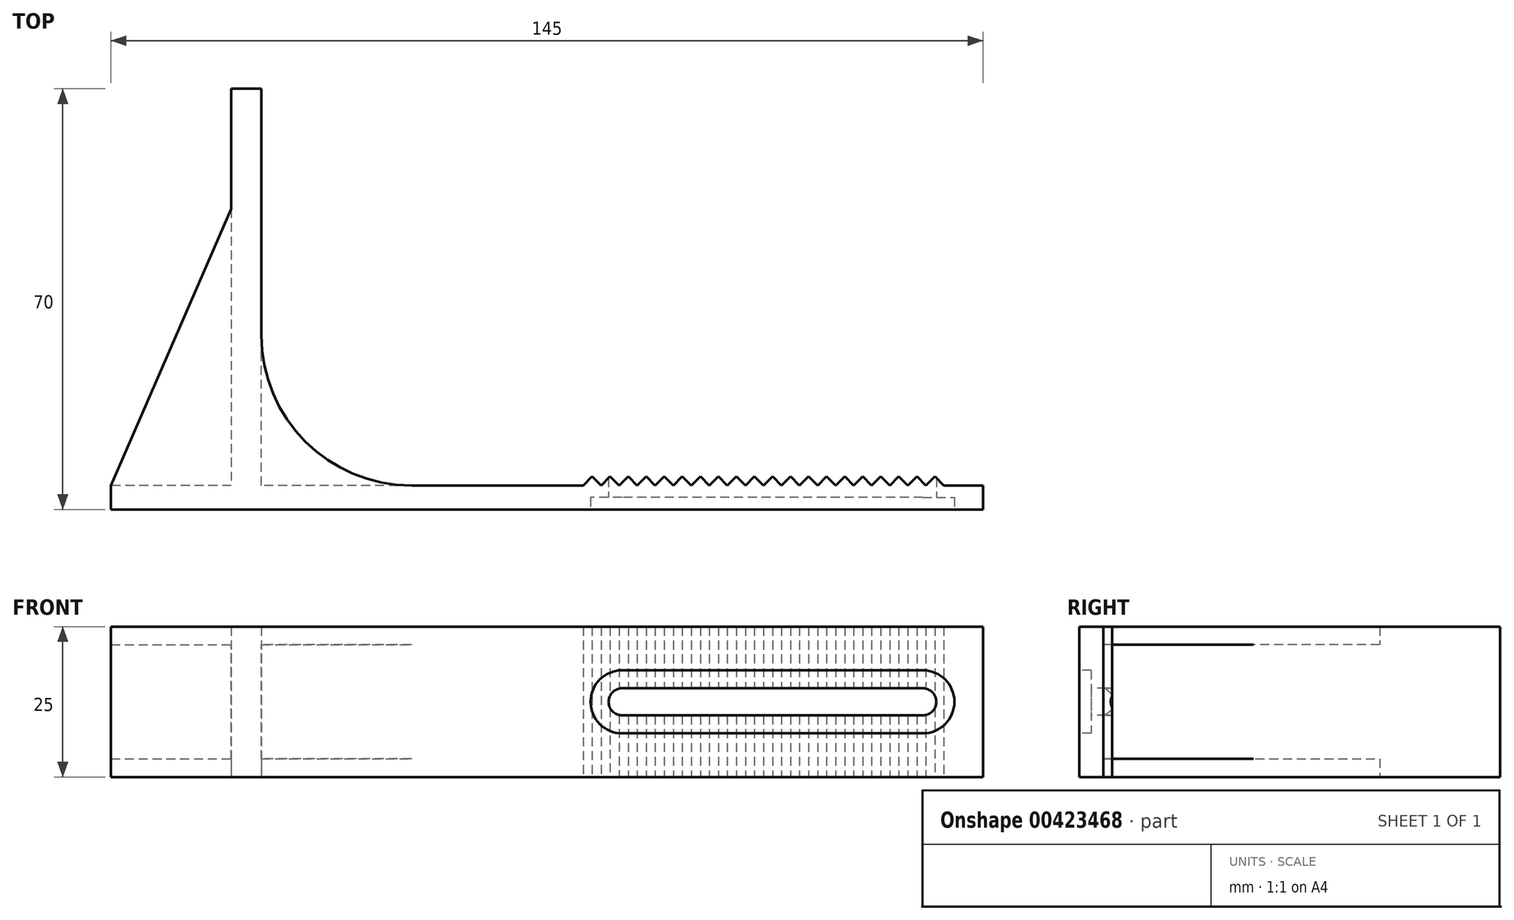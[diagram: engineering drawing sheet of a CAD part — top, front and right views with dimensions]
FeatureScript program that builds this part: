
annotation { "Feature Type Name" : "Feature", "Feature Type Description" : "" }
export const myFeature = defineFeature(function(context is Context, id is Id, definition is map)
    precondition{}
    {
        {
            var Q0;
            Q0=qCreatedBy(makeId("Top.planeOp"),FACE);
            var sketch = newSketch(context, id + "F0", { "sketchPlane" : qUnion([Q0])});
            skLineSegment(sketch, "E0.bottom", {"start": v(25, 0) * mm, "end": v(53.5, 0) * mm});
            skLineSegment(sketch, "E0.top", {"start": v(-25, -4) * mm, "end": v(120, -4) * mm});
            skLineSegment(sketch, "E0.right", {"start": v(120, 0) * mm, "end": v(120, -4) * mm});
            skLineSegment(sketch, "E1.top", {"start": v(0, 66) * mm, "end": v(-5, 66) * mm});
            skLineSegment(sketch, "E1.left", {"start": v(0, 25) * mm, "end": v(0, 66) * mm});
            skLineSegment(sketch, "E1.right", {"start": v(-5, 46) * mm, "end": v(-5, 66) * mm});
            skLineSegment(sketch, "E2", {"start": v(53.5, 0) * mm, "end": v(55, 1.5) * mm});
            skLineSegment(sketch, "E3", {"start": v(55, 1.5) * mm, "end": v(56.5, 0) * mm});
            skLineSegment(sketch, "E4.1.0.0", {"start": v(56.5, 0) * mm, "end": v(58, 1.5) * mm});
            skLineSegment(sketch, "E4.1.0.1", {"start": v(58, 1.5) * mm, "end": v(59.5, 0) * mm});
            skLineSegment(sketch, "E4.2.0.0", {"start": v(59.5, 0) * mm, "end": v(61, 1.5) * mm});
            skLineSegment(sketch, "E4.2.0.1", {"start": v(61, 1.5) * mm, "end": v(62.5, 0) * mm});
            skLineSegment(sketch, "E4.3.0.0", {"start": v(62.5, 0) * mm, "end": v(64, 1.5) * mm});
            skLineSegment(sketch, "E4.3.0.1", {"start": v(64, 1.5) * mm, "end": v(65.5, 0) * mm});
            skLineSegment(sketch, "E4.4.0.0", {"start": v(65.5, 0) * mm, "end": v(67, 1.5) * mm});
            skLineSegment(sketch, "E4.4.0.1", {"start": v(67, 1.5) * mm, "end": v(68.5, 0) * mm});
            skLineSegment(sketch, "E4.5.0.0", {"start": v(68.5, 0) * mm, "end": v(70, 1.5) * mm});
            skLineSegment(sketch, "E4.5.0.1", {"start": v(70, 1.5) * mm, "end": v(71.5, 0) * mm});
            skLineSegment(sketch, "E4.6.0.0", {"start": v(71.5, 0) * mm, "end": v(73, 1.5) * mm});
            skLineSegment(sketch, "E4.6.0.1", {"start": v(73, 1.5) * mm, "end": v(74.5, 0) * mm});
            skLineSegment(sketch, "E4.7.0.0", {"start": v(74.5, 0) * mm, "end": v(76, 1.5) * mm});
            skLineSegment(sketch, "E4.7.0.1", {"start": v(76, 1.5) * mm, "end": v(77.5, 0) * mm});
            skLineSegment(sketch, "E4.8.0.0", {"start": v(77.5, 0) * mm, "end": v(79, 1.5) * mm});
            skLineSegment(sketch, "E4.8.0.1", {"start": v(79, 1.5) * mm, "end": v(80.5, 0) * mm});
            skLineSegment(sketch, "E4.9.0.0", {"start": v(80.5, 0) * mm, "end": v(82, 1.5) * mm});
            skLineSegment(sketch, "E4.9.0.1", {"start": v(82, 1.5) * mm, "end": v(83.5, 0) * mm});
            skLineSegment(sketch, "E4.10.0.0", {"start": v(83.5, 0) * mm, "end": v(85, 1.5) * mm});
            skLineSegment(sketch, "E4.10.0.1", {"start": v(85, 1.5) * mm, "end": v(86.5, 0) * mm});
            skLineSegment(sketch, "E4.11.0.0", {"start": v(86.5, 0) * mm, "end": v(88, 1.5) * mm});
            skLineSegment(sketch, "E4.11.0.1", {"start": v(88, 1.5) * mm, "end": v(89.5, 0) * mm});
            skLineSegment(sketch, "E4.12.0.0", {"start": v(89.5, 0) * mm, "end": v(91, 1.5) * mm});
            skLineSegment(sketch, "E4.12.0.1", {"start": v(91, 1.5) * mm, "end": v(92.5, 0) * mm});
            skLineSegment(sketch, "E4.13.0.0", {"start": v(92.5, 0) * mm, "end": v(94, 1.5) * mm});
            skLineSegment(sketch, "E4.13.0.1", {"start": v(94, 1.5) * mm, "end": v(95.5, 0) * mm});
            skLineSegment(sketch, "E4.14.0.0", {"start": v(95.5, 0) * mm, "end": v(97, 1.5) * mm});
            skLineSegment(sketch, "E4.14.0.1", {"start": v(97, 1.5) * mm, "end": v(98.5, 0) * mm});
            skLineSegment(sketch, "E4.15.0.0", {"start": v(98.5, 0) * mm, "end": v(100, 1.5) * mm});
            skLineSegment(sketch, "E4.15.0.1", {"start": v(100, 1.5) * mm, "end": v(101.5, 0) * mm});
            skLineSegment(sketch, "E4.16.0.0", {"start": v(101.5, 0) * mm, "end": v(103, 1.5) * mm});
            skLineSegment(sketch, "E4.16.0.1", {"start": v(103, 1.5) * mm, "end": v(104.5, 0) * mm});
            skLineSegment(sketch, "E4.17.0.0", {"start": v(104.5, 0) * mm, "end": v(106, 1.5) * mm});
            skLineSegment(sketch, "E4.17.0.1", {"start": v(106, 1.5) * mm, "end": v(107.5, 0) * mm});
            skLineSegment(sketch, "E4.18.0.0", {"start": v(107.5, 0) * mm, "end": v(109, 1.5) * mm});
            skLineSegment(sketch, "E4.18.0.1", {"start": v(109, 1.5) * mm, "end": v(110.5, 0) * mm});
            skLineSegment(sketch, "E4.19.0.0", {"start": v(110.5, 0) * mm, "end": v(112, 1.5) * mm});
            skLineSegment(sketch, "E4.19.0.1", {"start": v(112, 1.5) * mm, "end": v(113.5, 0) * mm});
            skLineSegment(sketch, "E5.trimOffspring", {"start": v(113.5, 0) * mm, "end": v(120, 0) * mm});
            skPoint(sketch, "E6.orphan", {"position": v(62.5, 0) * mm});
            skPoint(sketch, "E7.orphan", {"position": v(65.5, 0) * mm});
            skLineSegment(sketch, "E8", {"start": v(-25, -4) * mm, "end": v(-25, 0) * mm});
            skLineSegment(sketch, "E9", {"start": v(-25, 0) * mm, "end": v(-5, 46) * mm});
            skPoint(sketch, "E10.visualSharp", {"position": v(0, 0) * mm});
            skArc(sketch, "E10.filletArc", {"start": v(0, 25) * mm, "mid": v(7.32, 7.32) * mm, "end": v(25, 0) * mm});
            skSolve(sketch);
        }
        {
            var Q0;
            Q0 = qSketchRegion(id + "F0", true);
            extrude(context, id + "F1", {"entities" : qUnion([Q0]), "depth" : 25 * mm, "offsetDistance" : 25 * mm});
        }
        {
            var Q0;
            Q0=makeQuery(id+"F1.opExtrude","SWEPT_FACE",FACE,{"disambiguationData":[OSD([sQuery(id+"F0.wireOp",EDGE,"E0.top")])]});
            var sketch = newSketch(context, id + "F2", { "sketchPlane" : qUnion([Q0])});
            skPoint(sketch, "E11", {"position": v(120, 12.5) * mm});
            skPoint(sketch, "E12", {"position": v(-25, 12.5) * mm});
            skLineSegment(sketch, "E13", {"start": v(-37.9, 12.5) * mm, "end": v(157.9, 12.5) * mm, "construction": true});
            skArc(sketch, "E14", {"start": v(110, 10.25) * mm, "mid": v(112.25, 12.5) * mm, "end": v(110, 14.75) * mm});
            skArc(sketch, "E15", {"start": v(60, 14.75) * mm, "mid": v(57.75, 12.5) * mm, "end": v(60, 10.25) * mm});
            skLineSegment(sketch, "E16", {"start": v(60, 14.75) * mm, "end": v(110, 14.75) * mm});
            skLineSegment(sketch, "E17", {"start": v(60, 10.25) * mm, "end": v(110, 10.25) * mm});
            skSolve(sketch);
        }
        {
            var Q0;
            Q0 = qSketchRegion(id + "F2", true);
            extrude(context, id + "F3", {"entities" : qUnion([Q0]), "operationType" : NewBodyOperationType.REMOVE, "endBound" : BoundingType.THROUGH_ALL, "oppositeDirection" : true, "depth" : 25 * mm, "offsetDistance" : 25 * mm});
        }
        {
            var Q0;
            Q0=makeQuery(id+"F1.opExtrude","SWEPT_FACE",FACE,{"disambiguationData":[OSD([sQuery(id+"F0.wireOp",EDGE,"E0.top")])]});
            var sketch = newSketch(context, id + "F4", { "sketchPlane" : qUnion([Q0])});
            skLineSegment(sketch, "E18.0", {"start": v(60, 10.25) * mm, "end": v(110, 10.25) * mm, "construction": true});
            skLineSegment(sketch, "E19.0", {"start": v(60, 14.75) * mm, "end": v(110, 14.75) * mm, "construction": true});
            skArc(sketch, "E20.0", {"start": v(110, 10.25) * mm, "mid": v(112.25, 12.5) * mm, "end": v(110, 14.75) * mm, "construction": true});
            skArc(sketch, "E21.0", {"start": v(60, 14.75) * mm, "mid": v(57.75, 12.5) * mm, "end": v(60, 10.25) * mm, "construction": true});
            skLineSegment(sketch, "E22.0", {"start": v(60, 17.75) * mm, "end": v(110, 17.75) * mm});
            skArc(sketch, "E22.1", {"start": v(60, 17.75) * mm, "mid": v(54.75, 12.5) * mm, "end": v(60, 7.25) * mm});
            skLineSegment(sketch, "E22.2", {"start": v(60, 7.25) * mm, "end": v(110, 7.25) * mm});
            skArc(sketch, "E22.3", {"start": v(110, 7.25) * mm, "mid": v(115.25, 12.5) * mm, "end": v(110, 17.75) * mm});
            skSolve(sketch);
        }
        {
            var Q0;
            Q0 = qSketchRegion(id + "F4", true);
            extrude(context, id + "F5", {"entities" : qUnion([Q0]), "operationType" : NewBodyOperationType.REMOVE, "oppositeDirection" : true, "depth" : 2 * mm, "offsetDistance" : 25 * mm});
        }
        {
            var Q0;
            Q0=makeQuery(id+"F1.opExtrude","SWEPT_FACE",FACE,{"disambiguationData":[OSD([sQuery(id+"F0.wireOp",EDGE,"E8")])]});
            var sketch = newSketch(context, id + "F6", { "sketchPlane" : qUnion([Q0])});
            skLineSegment(sketch, "E23.bottom", {"start": v(0, 22) * mm, "end": v(-46, 22) * mm});
            skLineSegment(sketch, "E23.top", {"start": v(0, 3) * mm, "end": v(-46, 3) * mm});
            skLineSegment(sketch, "E23.left", {"start": v(0, 22) * mm, "end": v(0, 3) * mm});
            skLineSegment(sketch, "E23.right", {"start": v(-46, 22) * mm, "end": v(-46, 3) * mm});
            skSolve(sketch);
        }
        {
            var Q0;
            Q0 = qSketchRegion(id + "F6", true);
            var Q1;
            Q1=makeQuery(id+"F1.opExtrude","SWEPT_FACE",FACE,{"disambiguationData":[OSD([sQuery(id+"F0.wireOp",EDGE,"E1.right")])]});
            extrude(context, id + "F7", {"entities" : qUnion([Q0]), "operationType" : NewBodyOperationType.REMOVE, "endBound" : BoundingType.UP_TO_SURFACE, "oppositeDirection" : true, "depth" : 25 * mm, "endBoundEntityFace" : qUnion([Q1]), "offsetDistance" : 25 * mm});
        }
        {
            var Q0;
            Q0=makeQuery(id+"F1.opExtrude","SWEPT_FACE",FACE,{"disambiguationData":[OSD([sQuery(id+"F0.wireOp",EDGE,"E1.top")])]});
            var sketch = newSketch(context, id + "F8", { "sketchPlane" : qUnion([Q0])});
            skLineSegment(sketch, "E24.bottom", {"start": v(0, 22) * mm, "end": v(-25, 22) * mm});
            skLineSegment(sketch, "E24.top", {"start": v(0, 3) * mm, "end": v(-25, 3) * mm});
            skLineSegment(sketch, "E24.left", {"start": v(0, 22) * mm, "end": v(0, 3) * mm});
            skLineSegment(sketch, "E24.right", {"start": v(-25, 22) * mm, "end": v(-25, 3) * mm});
            skSolve(sketch);
        }
        {
            var Q0;
            Q0 = qSketchRegion(id + "F8", true);
            var Q1;
            Q1=makeQuery(id+"F1.opExtrude","SWEPT_FACE",FACE,{"disambiguationData":[OSD([sQuery(id+"F0.wireOp",EDGE,"E0.bottom")])]});
            extrude(context, id + "F9", {"entities" : qUnion([Q0]), "operationType" : NewBodyOperationType.REMOVE, "endBound" : BoundingType.UP_TO_SURFACE, "oppositeDirection" : true, "depth" : 25 * mm, "endBoundEntityFace" : qUnion([Q1]), "offsetDistance" : 25 * mm});
        }
    });
